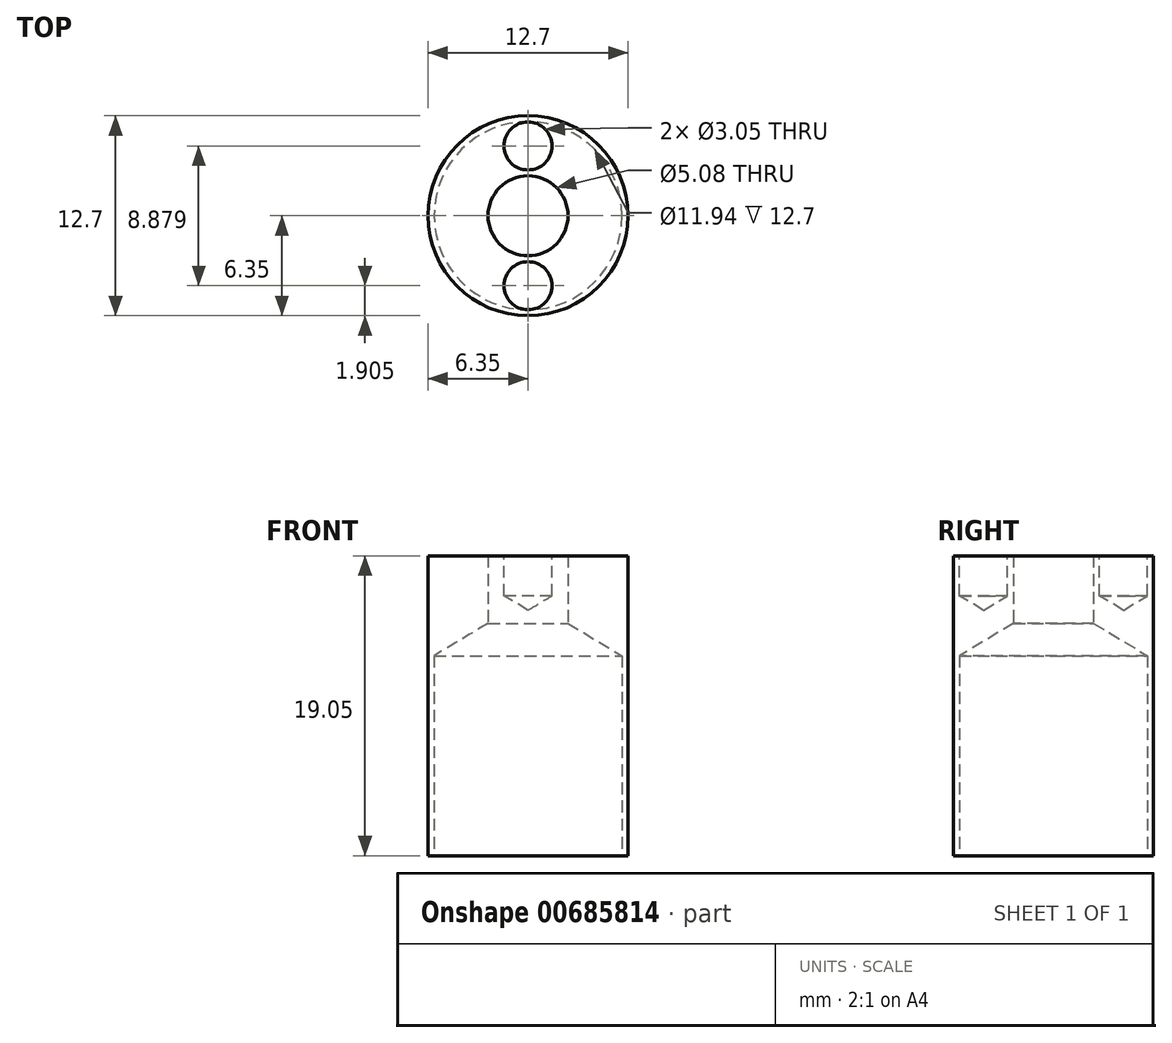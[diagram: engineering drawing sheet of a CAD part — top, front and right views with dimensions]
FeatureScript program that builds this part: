
annotation { "Feature Type Name" : "Feature", "Feature Type Description" : "" }
export const myFeature = defineFeature(function(context is Context, id is Id, definition is map)
    precondition{}
    {
        {
            var Q0;
            Q0=qCreatedBy(makeId("Top.planeOp"),FACE);
            var sketch = newSketch(context, id + "F0", { "sketchPlane" : qUnion([Q0])});
            skCircle(sketch, "E0", {"center": v(0, 0) * mm, "radius": 6.35 * mm});
            skSolve(sketch);
        }
        {
            var Q0;
            Q0=makeQuery(id+"F0.imprint","IMPRINT",FACE,{"disambiguationData":[TD([[makeQuery(id+"F0.imprint","IMPRINT",EDGE,{"derivedFrom":sQuery(id+"F0.wireOp",EDGE,"E0")}),1.0]])]});
            extrude(context, id + "F1", {"entities" : qUnion([Q0]), "depth" : 19.05 * mm, "offsetDistance" : 25.4 * mm});
        }
        {
            var Q0;
            Q0=qCreatedBy(makeId("Top.planeOp"),FACE);
            var sketch = newSketch(context, id + "F2", { "sketchPlane" : qUnion([Q0])});
            skPoint(sketch, "E1", {"position": v(0, 0) * mm});
            skSolve(sketch);
        }
        {
            var Q0;
            Q0=sQuery(id+"F2.wireOp",VERTEX,"E1");
            var Q1;
            Q1=makeQuery(id+"F1.opExtrude","SWEPT_BODY",BODY,{"disambiguationData":[OSD([sQuery(id+"F0.wireOp",EDGE,"E0")])]});
            hole(context, id + "F3", {"style" : HoleStyle.SIMPLE, "endStyle" : HoleEndStyle.THROUGH, "oppositeDirection" : true, "holeDiameter" : 5.08 * mm, "majorDiameter" : 6.35 * mm, "isTappedThrough" : true, "tappedDepth" : 12.7 * mm, "tapClearance" : 3, "locations" : qUnion([Q0]), "scope" : qUnion([Q1])});
        }
        {
            var Q0;
            Q0=makeQuery(id+"F1.opExtrude","CAP_FACE",FACE,{"disambiguationData":[OSD([sQuery(id+"F0.wireOp",EDGE,"E0")])],"isStart":false});
            var sketch = newSketch(context, id + "F4", { "sketchPlane" : qUnion([Q0])});
            skPoint(sketch, "E2", {"position": v(0, 4.43) * mm});
            skSolve(sketch);
        }
        {
            var Q0;
            Q0=makeQuery(id+"F1.opExtrude","CAP_FACE",FACE,{"disambiguationData":[OSD([sQuery(id+"F0.wireOp",EDGE,"E0")])],"isStart":false});
            var sketch = newSketch(context, id + "F5", { "sketchPlane" : qUnion([Q0])});
            skPoint(sketch, "E3", {"position": v(0, -4.45) * mm});
            skSolve(sketch);
        }
        {
            var Q0;
            {var subQ0=sQuery(id+"F0.wireOp",EDGE,"E0");Q0=makeQuery(id+"F4.imprint","IMPRINT",FACE,{"disambiguationData":[TD([[makeQuery(id+"F4.imprint","IMPRINT",EDGE,{"derivedFrom":makeQuery(id+"F1.opExtrude","CAP_EDGE",EDGE,{"disambiguationData":[OSD([subQ0])],"isStart":false})}),1.0]])]});}
            var sketch = newSketch(context, id + "F6", { "sketchPlane" : qUnion([Q0])});
            skCircle(sketch, "E4", {"center": v(0, 4.4) * mm, "radius": 1.52 * mm});
            skSolve(sketch);
        }
        {
            var Q0;
            Q0=sQuery(id+"F6.wireOp",EDGE,"E4");
            extrude(context, id + "F7", {"bodyType" : ToolBodyType.SURFACE, "surfaceEntities" : qUnion([Q0]), "oppositeDirection" : true, "depth" : 3.05 * mm, "offsetDistance" : 25.4 * mm});
        }
        {
            var Q0;
            Q0=sQuery(id+"F4.wireOp",VERTEX,"E2");
            var Q1;
            Q1=makeQuery(id+"F1.opExtrude","SWEPT_BODY",BODY,{"disambiguationData":[OSD([sQuery(id+"F0.wireOp",EDGE,"E0")])]});
            hole(context, id + "F8", {"style" : HoleStyle.SIMPLE, "endStyle" : HoleEndStyle.BLIND, "holeDiameter" : 3.05 * mm, "majorDiameter" : 6.35 * mm, "holeDepth" : 2.54 * mm, "isTappedThrough" : true, "tappedDepth" : 12.7 * mm, "tapClearance" : 3, "locations" : qUnion([Q0]), "scope" : qUnion([Q1])});
        }
        {
            var Q0;
            Q0=sQuery(id+"F5.wireOp",VERTEX,"E3");
            var Q1;
            Q1=makeQuery(id+"F1.opExtrude","SWEPT_BODY",BODY,{"disambiguationData":[OSD([sQuery(id+"F0.wireOp",EDGE,"E0")])]});
            hole(context, id + "F9", {"style" : HoleStyle.SIMPLE, "endStyle" : HoleEndStyle.BLIND, "holeDiameter" : 3.05 * mm, "majorDiameter" : 6.35 * mm, "holeDepth" : 2.54 * mm, "isTappedThrough" : true, "tappedDepth" : 12.7 * mm, "tapClearance" : 3, "locations" : qUnion([Q0]), "scope" : qUnion([Q1])});
        }
        {
            var Q0;
            Q0=makeQuery(id+"F1.opExtrude","CAP_FACE",FACE,{"disambiguationData":[OSD([sQuery(id+"F0.wireOp",EDGE,"E0")])],"isStart":true});
            var sketch = newSketch(context, id + "F10", { "sketchPlane" : qUnion([Q0])});
            skPoint(sketch, "E5", {"position": v(0, 0) * mm});
            skSolve(sketch);
        }
        {
            var Q0;
            Q0=sQuery(id+"F10.wireOp",VERTEX,"E5");
            var Q1;
            Q1=makeQuery(id+"F1.opExtrude","SWEPT_BODY",BODY,{"disambiguationData":[OSD([sQuery(id+"F0.wireOp",EDGE,"E0")])]});
            hole(context, id + "F11", {"style" : HoleStyle.SIMPLE, "endStyle" : HoleEndStyle.BLIND, "holeDiameter" : 11.94 * mm, "majorDiameter" : 6.35 * mm, "holeDepth" : 12.7 * mm, "isTappedThrough" : true, "tappedDepth" : 12.7 * mm, "tapClearance" : 3, "locations" : qUnion([Q0]), "scope" : qUnion([Q1])});
        }
    });
